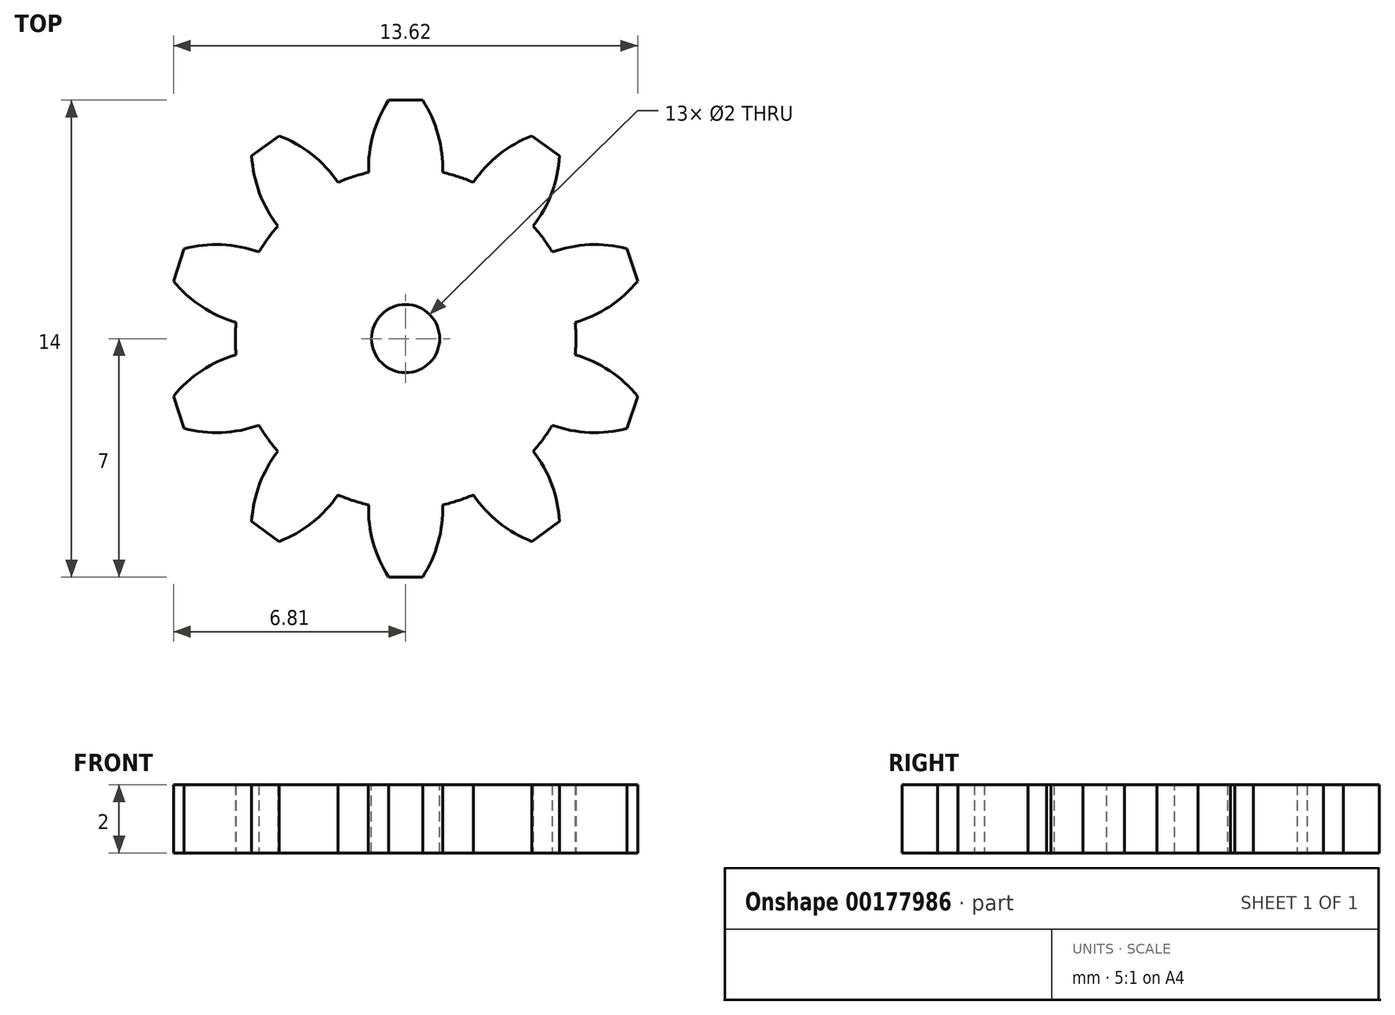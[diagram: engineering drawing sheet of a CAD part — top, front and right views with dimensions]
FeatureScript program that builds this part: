
annotation { "Feature Type Name" : "Feature", "Feature Type Description" : "" }
export const myFeature = defineFeature(function(context is Context, id is Id, definition is map)
    precondition{}
    {
        {
            var Q0;
            Q0=qCreatedBy(makeId("Top.planeOp"),FACE);
            var sketch = newSketch(context, id + "F0", { "sketchPlane" : qUnion([Q0])});
            skCircle(sketch, "E0", {"center": v(0, 0) * mm, "radius": 5 * mm});
            skLineSegment(sketch, "E1", {"start": v(0, 0) * mm, "end": v(0, 5) * mm, "construction": true});
            skLineSegment(sketch, "E2", {"start": v(0, 7) * mm, "end": v(-0.5, 7) * mm});
            skArc(sketch, "E3", {"start": v(-0.5, 7) * mm, "mid": v(-0.96, 5.98) * mm, "end": v(-1.09, 4.88) * mm});
            skLineSegment(sketch, "E4.MirrorCS", {"start": v(0, 7) * mm, "end": v(0.5, 7) * mm});
            skArc(sketch, "E5.MirrorCS", {"start": v(0.5, 7) * mm, "mid": v(0.96, 5.98) * mm, "end": v(1.09, 4.88) * mm});
            skArc(sketch, "E6.1.0", {"start": v(-4.52, 5.37) * mm, "mid": v(-4.3, 4.28) * mm, "end": v(-3.75, 3.3) * mm});
            skLineSegment(sketch, "E6.1.1", {"start": v(-4.11, 5.66) * mm, "end": v(-4.52, 5.37) * mm});
            skLineSegment(sketch, "E6.1.2", {"start": v(-4.11, 5.66) * mm, "end": v(-3.7, 5.96) * mm});
            skArc(sketch, "E6.1.3", {"start": v(-3.7, 5.96) * mm, "mid": v(-2.75, 5.4) * mm, "end": v(-1.99, 4.59) * mm});
            skArc(sketch, "E6.2.0", {"start": v(-6.81, 1.69) * mm, "mid": v(-5.99, 0.94) * mm, "end": v(-4.98, 0.47) * mm});
            skLineSegment(sketch, "E6.2.1", {"start": v(-6.66, 2.16) * mm, "end": v(-6.81, 1.69) * mm});
            skLineSegment(sketch, "E6.2.2", {"start": v(-6.66, 2.16) * mm, "end": v(-6.5, 2.64) * mm});
            skArc(sketch, "E6.2.3", {"start": v(-6.5, 2.64) * mm, "mid": v(-5.4, 2.76) * mm, "end": v(-4.3, 2.54) * mm});
            skArc(sketch, "E6.3.0", {"start": v(-6.5, -2.64) * mm, "mid": v(-5.4, -2.76) * mm, "end": v(-4.3, -2.54) * mm});
            skLineSegment(sketch, "E6.3.1", {"start": v(-6.66, -2.16) * mm, "end": v(-6.5, -2.64) * mm});
            skLineSegment(sketch, "E6.3.2", {"start": v(-6.66, -2.16) * mm, "end": v(-6.81, -1.69) * mm});
            skArc(sketch, "E6.3.3", {"start": v(-6.81, -1.69) * mm, "mid": v(-5.99, -0.94) * mm, "end": v(-4.98, -0.47) * mm});
            skArc(sketch, "E6.4.0", {"start": v(-3.7, -5.96) * mm, "mid": v(-2.75, -5.4) * mm, "end": v(-1.99, -4.59) * mm});
            skLineSegment(sketch, "E6.4.1", {"start": v(-4.11, -5.66) * mm, "end": v(-3.7, -5.96) * mm});
            skLineSegment(sketch, "E6.4.2", {"start": v(-4.11, -5.66) * mm, "end": v(-4.52, -5.37) * mm});
            skArc(sketch, "E6.4.3", {"start": v(-4.52, -5.37) * mm, "mid": v(-4.3, -4.28) * mm, "end": v(-3.75, -3.3) * mm});
            skArc(sketch, "E6.5.0", {"start": v(0.5, -7) * mm, "mid": v(0.96, -5.98) * mm, "end": v(1.09, -4.88) * mm});
            skLineSegment(sketch, "E6.5.1", {"start": v(0, -7) * mm, "end": v(0.5, -7) * mm});
            skLineSegment(sketch, "E6.5.2", {"start": v(0, -7) * mm, "end": v(-0.5, -7) * mm});
            skArc(sketch, "E6.5.3", {"start": v(-0.5, -7) * mm, "mid": v(-0.96, -5.98) * mm, "end": v(-1.09, -4.88) * mm});
            skArc(sketch, "E6.6.0", {"start": v(4.52, -5.37) * mm, "mid": v(4.3, -4.28) * mm, "end": v(3.75, -3.3) * mm});
            skLineSegment(sketch, "E6.6.1", {"start": v(4.11, -5.66) * mm, "end": v(4.52, -5.37) * mm});
            skLineSegment(sketch, "E6.6.2", {"start": v(4.11, -5.66) * mm, "end": v(3.7, -5.96) * mm});
            skArc(sketch, "E6.6.3", {"start": v(3.7, -5.96) * mm, "mid": v(2.75, -5.4) * mm, "end": v(1.99, -4.59) * mm});
            skArc(sketch, "E6.7.0", {"start": v(6.81, -1.69) * mm, "mid": v(5.99, -0.94) * mm, "end": v(4.98, -0.47) * mm});
            skLineSegment(sketch, "E6.7.1", {"start": v(6.66, -2.16) * mm, "end": v(6.81, -1.69) * mm});
            skLineSegment(sketch, "E6.7.2", {"start": v(6.66, -2.16) * mm, "end": v(6.5, -2.64) * mm});
            skArc(sketch, "E6.7.3", {"start": v(6.5, -2.64) * mm, "mid": v(5.4, -2.76) * mm, "end": v(4.3, -2.54) * mm});
            skArc(sketch, "E6.8.0", {"start": v(6.5, 2.64) * mm, "mid": v(5.4, 2.76) * mm, "end": v(4.3, 2.54) * mm});
            skLineSegment(sketch, "E6.8.1", {"start": v(6.66, 2.16) * mm, "end": v(6.5, 2.64) * mm});
            skLineSegment(sketch, "E6.8.2", {"start": v(6.66, 2.16) * mm, "end": v(6.81, 1.69) * mm});
            skArc(sketch, "E6.8.3", {"start": v(6.81, 1.69) * mm, "mid": v(5.99, 0.94) * mm, "end": v(4.98, 0.47) * mm});
            skArc(sketch, "E6.9.0", {"start": v(3.7, 5.96) * mm, "mid": v(2.75, 5.4) * mm, "end": v(1.99, 4.59) * mm});
            skLineSegment(sketch, "E6.9.1", {"start": v(4.11, 5.66) * mm, "end": v(3.7, 5.96) * mm});
            skLineSegment(sketch, "E6.9.2", {"start": v(4.11, 5.66) * mm, "end": v(4.52, 5.37) * mm});
            skArc(sketch, "E6.9.3", {"start": v(4.52, 5.37) * mm, "mid": v(4.3, 4.28) * mm, "end": v(3.75, 3.3) * mm});
            skSolve(sketch);
        }
        {
            var Q0;
            Q0=qSketchRegion(id+"F0",true);
            extrude(context, id + "F1", {"entities" : qUnion([Q0]), "depth" : 2 * mm});
        }
        {
            var Q0;
            Q0=makeQuery(id+"F1.opExtrude","CAP_FACE",FACE,{"disambiguationData":[OSD([sQuery(id+"F0.wireOp",EDGE,"E0"),sQuery(id+"F0.wireOp",EDGE,"E2"),sQuery(id+"F0.wireOp",EDGE,"E3"),sQuery(id+"F0.wireOp",EDGE,"E4.MirrorCS"),sQuery(id+"F0.wireOp",EDGE,"E5.MirrorCS"),sQuery(id+"F0.wireOp",EDGE,"E6.1.0"),sQuery(id+"F0.wireOp",EDGE,"E6.1.1"),sQuery(id+"F0.wireOp",EDGE,"E6.1.2"),sQuery(id+"F0.wireOp",EDGE,"E6.1.3"),sQuery(id+"F0.wireOp",EDGE,"E6.2.0"),sQuery(id+"F0.wireOp",EDGE,"E6.2.1"),sQuery(id+"F0.wireOp",EDGE,"E6.2.2"),sQuery(id+"F0.wireOp",EDGE,"E6.2.3"),sQuery(id+"F0.wireOp",EDGE,"E6.3.0"),sQuery(id+"F0.wireOp",EDGE,"E6.3.1"),sQuery(id+"F0.wireOp",EDGE,"E6.3.2"),sQuery(id+"F0.wireOp",EDGE,"E6.3.3"),sQuery(id+"F0.wireOp",EDGE,"E6.4.0"),sQuery(id+"F0.wireOp",EDGE,"E6.4.1"),sQuery(id+"F0.wireOp",EDGE,"E6.4.2"),sQuery(id+"F0.wireOp",EDGE,"E6.4.3"),sQuery(id+"F0.wireOp",EDGE,"E6.5.0"),sQuery(id+"F0.wireOp",EDGE,"E6.5.1"),sQuery(id+"F0.wireOp",EDGE,"E6.5.2"),sQuery(id+"F0.wireOp",EDGE,"E6.5.3"),sQuery(id+"F0.wireOp",EDGE,"E6.6.0"),sQuery(id+"F0.wireOp",EDGE,"E6.6.1"),sQuery(id+"F0.wireOp",EDGE,"E6.6.2"),sQuery(id+"F0.wireOp",EDGE,"E6.6.3"),sQuery(id+"F0.wireOp",EDGE,"E6.7.0"),sQuery(id+"F0.wireOp",EDGE,"E6.7.1"),sQuery(id+"F0.wireOp",EDGE,"E6.7.2"),sQuery(id+"F0.wireOp",EDGE,"E6.7.3"),sQuery(id+"F0.wireOp",EDGE,"E6.8.0"),sQuery(id+"F0.wireOp",EDGE,"E6.8.1"),sQuery(id+"F0.wireOp",EDGE,"E6.8.2"),sQuery(id+"F0.wireOp",EDGE,"E6.8.3"),sQuery(id+"F0.wireOp",EDGE,"E6.9.0"),sQuery(id+"F0.wireOp",EDGE,"E6.9.1"),sQuery(id+"F0.wireOp",EDGE,"E6.9.2"),sQuery(id+"F0.wireOp",EDGE,"E6.9.3"),sQuery(id+"F0.wireOp",EDGE,"E6.10.0"),sQuery(id+"F0.wireOp",EDGE,"E6.10.1"),sQuery(id+"F0.wireOp",EDGE,"E6.10.2"),sQuery(id+"F0.wireOp",EDGE,"E6.10.3"),sQuery(id+"F0.wireOp",EDGE,"E6.11.0"),sQuery(id+"F0.wireOp",EDGE,"E6.11.1"),sQuery(id+"F0.wireOp",EDGE,"E6.11.2"),sQuery(id+"F0.wireOp",EDGE,"E6.11.3"),sQuery(id+"F0.wireOp",EDGE,"E6.12.0"),sQuery(id+"F0.wireOp",EDGE,"E6.12.1"),sQuery(id+"F0.wireOp",EDGE,"E6.12.2"),sQuery(id+"F0.wireOp",EDGE,"E6.12.3"),sQuery(id+"F0.wireOp",EDGE,"E6.13.0"),sQuery(id+"F0.wireOp",EDGE,"E6.13.1"),sQuery(id+"F0.wireOp",EDGE,"E6.13.2"),sQuery(id+"F0.wireOp",EDGE,"E6.13.3"),sQuery(id+"F0.wireOp",EDGE,"E6.14.0"),sQuery(id+"F0.wireOp",EDGE,"E6.14.1"),sQuery(id+"F0.wireOp",EDGE,"E6.14.2"),sQuery(id+"F0.wireOp",EDGE,"E6.14.3"),sQuery(id+"F0.wireOp",EDGE,"E6.15.0"),sQuery(id+"F0.wireOp",EDGE,"E6.15.1"),sQuery(id+"F0.wireOp",EDGE,"E6.15.2"),sQuery(id+"F0.wireOp",EDGE,"E6.15.3")])],"isStart":false});
            var sketch = newSketch(context, id + "F2", { "sketchPlane" : qUnion([Q0])});
            skCircle(sketch, "E7", {"center": v(0, 0) * mm, "radius": 1 * mm});
            skSolve(sketch);
        }
        {
            var Q0;
            Q0=makeQuery(id+"F2.imprint","IMPRINT",FACE,{"disambiguationData":[TD([[makeQuery(id+"F2.imprint","IMPRINT",EDGE,{"derivedFrom":sQuery(id+"F2.wireOp",EDGE,"E7")}),1.0]])]});
            extrude(context, id + "F3", {"entities" : qUnion([Q0]), "operationType" : NewBodyOperationType.REMOVE, "endBound" : BoundingType.THROUGH_ALL, "oppositeDirection" : true, "depth" : 25 * mm});
        }
    });
